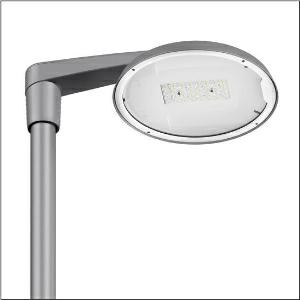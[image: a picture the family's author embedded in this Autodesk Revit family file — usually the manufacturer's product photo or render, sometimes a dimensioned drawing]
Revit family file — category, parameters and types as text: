
# Revit family: dl_r__50_iq_mini___st0_5a_5xa248b31f08ge_dbc8
name_source: partatom
category: Lighting Fixtures
units: mm (PartAtom-declared; Revit-internal decimal feet)

## family parameters
Cut with Voids When Loaded = No
Host = Face
Light Source = No
Part Type = Normal
Room Calculation Point = No
Round Connector Dimension = Use Diameter
Shared = No

## types (1)
- --- (1 x LED, 5190 lm, 32.7 W, 3000K)
    Apparent Load = 33 VA
    CIE Flux Codes = 41 75 97 100 100
    Color Rendering = 70
    Color Temperature = 3000K
    Default Elevation = 1800 mm
    Description = DL® 50 iQ mini, mast luminaire, primary light control with lens, of PMMA, primary optical cover: cover, of toughened safety glass, transparent, light distribution: ST0.5a, light emission: direct distribution, primary light characteristic: asymmetric, installation type: side-entry, post-top, LED, High Power LED, rated luminous flux: 5.190lm, luminous efficacy: 159lm/W, light colour: 730, colour temperature: 3000K, control: optimised constant luminous flux control (CLO 2.0), Desk-Remote (wireless, voltage-free reading and setting of iQ features in the workshop via application-optimized NFC function/RFID function), Light-Fading, Smart-Wire, Night-Set, Lumen-Switch, Temp-Guard, Auto-Match, Street-Remote, mains connection: 230..240V, AC, 50/60Hz, connection cable pre-assembled, cable length: 6,5m, start of lifetime: 33W, end of service life: 34W, reduction: 16W, luminaire housing, of diecast aluminium, powder-coated, Siteco® metallic grey (DB 702S), inclination adjustable: 0°, 5°, 10° (post-top) | 0°, -5°, -10°, -15° (side-entry), please order mast post-top element or mast side-entry element separately, diameter: 500mm, height: 115mm, post-top: for spigot size d x l = 76 x 100mm; with reducer (optional accessory) 60 x 100mm | side-entry: for spigot size d x l = 60 x 100mm; with reducer (optional accessory) 42 x 100mm, protection rating (complete): IP66, insulation class (complete): insulation class II (safety insulation), certification: CE, ENEC, VDE, impact resistance: IK08, permissible operating ambient temperature for outdoor applications: -25..+40°C, standard-compliant lighting for roads and squares, packaging unit: 1 piece

Light Distribution: ST0.5a
    Height = 115 mm
    Lamp = 1 x LED
    Lamp Light Flux = 5190 lm
    Lamp Power = 32.7 W
    Lamp count = 1
    Length = 500 mm
    Luminous efficacy = 159 lm/W
    Manufacturer = Siteco
    ModVariant = No
    Model = 5XA248B31F08GE
    Number of Poles = 1
    OnlyDefault = Yes
    Power Factor = 1
    Product Name = DL® 50 iQ mini | ST0.5a
    Product group = mast luminaire | pylon top
    ProductGroupID = 6100
    Protection Class = Protection class II
    Protection Degree = IP 66
    RLX_Detail_Level = 1
    RLX_Emergency_Light_Flux = 0 lm
    RLX_Emergency_Type = 0
    RLX_Emergency_Type_DB = No
    RlxData = <blob elided: 127169 chars, md5=e08751a7>
    Socket = socket
    Standby Power = 0 W
    System Light Flux = 5190 lm
    System Power = 33 W
    Type Comments = factory setting: luminous flux: 100 % | dim-lin: 254 | 340 mA
    Type Image = l_1251794.jpg
    URL = http://relux.com
    VarID = @adj_092669
    Voltage = 0 V
    Weight = 0.00 kg
    Width = 0 mm  [stored 0 ft]

note: [stored X ft] marks values corroborated as IEEE doubles in the binary element streams (Revit-internal decimal feet)

## geometry (parser evidence)
native form markers: Blend x4, Sweep x11
no freeform markers — native parametric forms only
